# Revit family: L10 Premium Cleverfit Pro LED Exit_Wall Hosted_R15
name_source: partatom
category: Lighting Fixtures
revit_build: Autodesk Revit 2015 (Build: 20150303_1515(x64)
units: mm (PartAtom-declared; Revit-internal decimal feet)

## types (1)
- DCFPRO
    AS2293 = C0=D4, C90=E8
    Apparent Load = 4 VA
    Ballast = Electronic
    Charging Method = Constant Current (16hrs), Pulse Charge (standby)
    Color Filter = 16777215
    Construction = Fire-retardant PC/ABS body with Polycarbonate Diffusers
    Diffuser = All directional inserts included in the box
    Dimming Lamp Color Temperature Shift = <None>
    Emit Shape Visible in Rendering = No
    Emit from Circle Diameter = 610 mm
    Height = 214 mm  [stored 0.7021 ft]
    IP Rating = IP20
    Lamp = 2 x LED 100,000 hours
    Length = 367 mm  [stored 1.20407 ft]
    Mounting = Surface Mount. Single Side Wall. Single or Double Side Ceiling.
    Operating Mode = Maintained
    Operating Temperature = 10 to +40°C
    Operating Voltage = 240.00 V
    Photometric Web File = ll18240 - LCFPRO-ZW.IES
    Power Consumption = 3.70 W
    Sign Height = 3 mm  [stored 0.00984252 ft]
    Sign Length = 353 mm  [stored 1.15814 ft]
    Sign Width = 178 mm  [stored 0.58399 ft]
    Testing System = Clever-test
    Tilt Angle = 90.00°
    Viewing Distance = 24000 mm  [stored 78.7402 ft]
    Wattage Comments = Standby
    Width = 72 mm  [stored 0.23622 ft]

note: [stored X ft] marks values corroborated as IEEE doubles in the binary element streams (Revit-internal decimal feet)

## geometry (parser evidence)
native form markers: Sweep x8
no freeform markers — native parametric forms only
